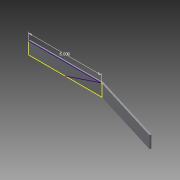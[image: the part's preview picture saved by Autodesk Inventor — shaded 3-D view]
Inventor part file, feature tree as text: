
AUTODESK INVENTOR PART (.ipt)
format: ipt  version: 2013 (Build 170138000, 138)  size: 98,304 bytes
history: native  units: in
note: dims shown in document units (in); Inventor stores cm internally (conversion verified against a paired STEP export)
features: sheet_metal_op x4, sketch x3, other x2
ambient origin geometry x8: Origin, YZ Plane, XZ Plane, XY Plane, X Axis, Y Axis, Z Axis, Center Point
bodies: Solid1 (feature_tree)
feature tree (9):
  sheet_metal_op  "Face1"
  sketch  "Sketch2"  dims[d1=1.0in]
  sheet_metal_op  "Flange1"
  sketch  "Sketch1"  dims[d0=6.067in]
  other  "Plate1"
  sketch  "Sketch3"  dims[d2=0.125in d3=6.0in d4=0.125in d5=0.0625in d6=0.25in d7=0.125in d8=6.0in d9=0.1172in d10=0.05in d11=0.5in d12=0.125in d13=0.125in]
  other  "Plate2"
  sheet_metal_op  "Bend1"
  sheet_metal_op  "Corner1"
